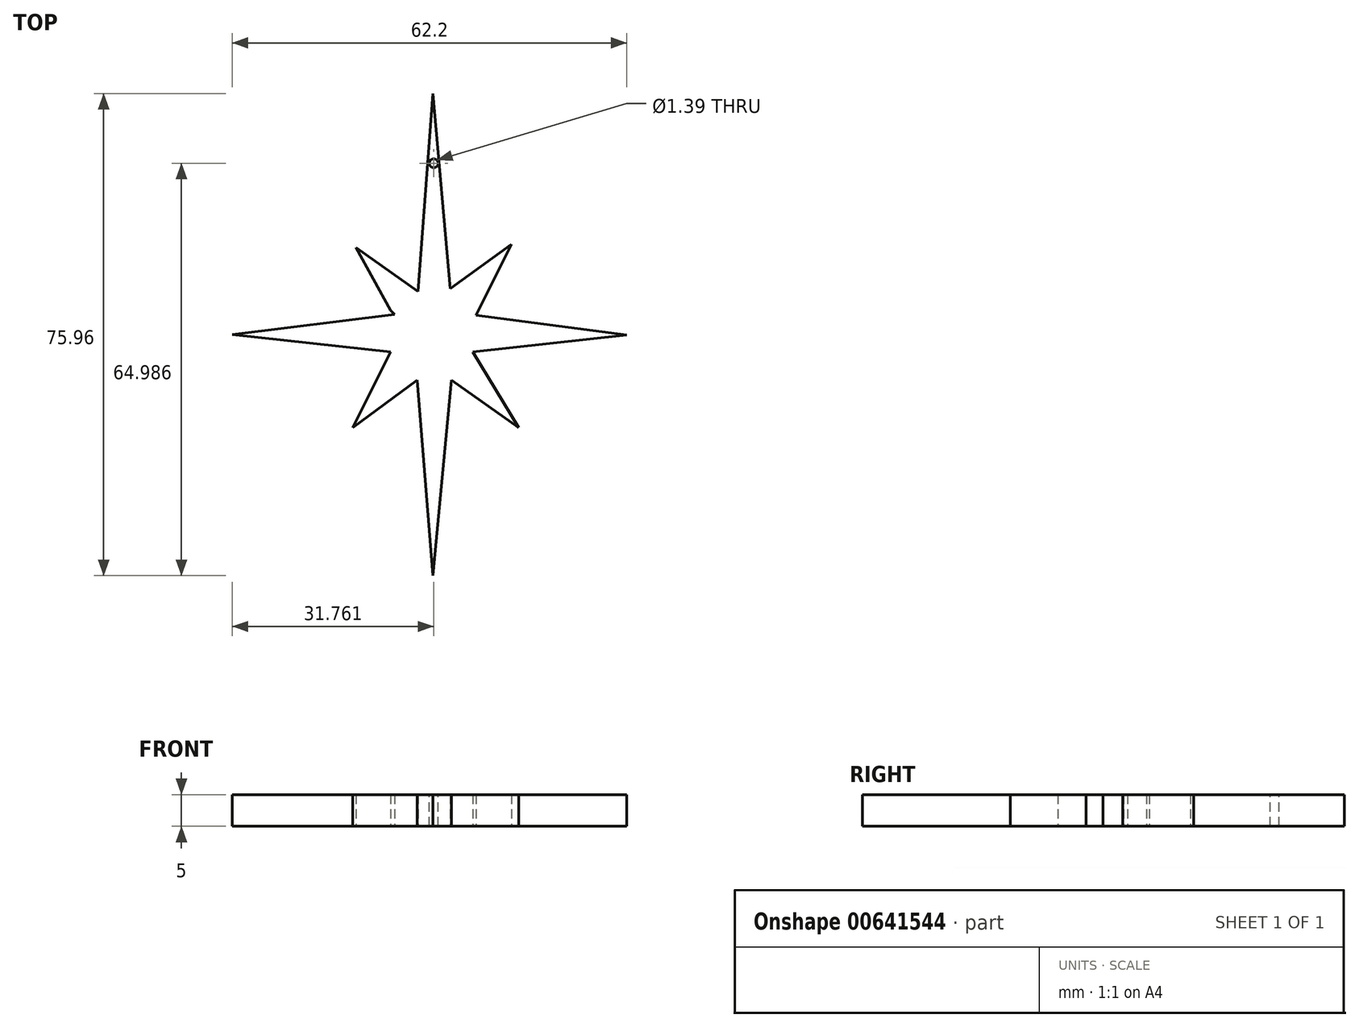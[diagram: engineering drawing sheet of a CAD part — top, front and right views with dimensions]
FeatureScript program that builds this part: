
annotation { "Feature Type Name" : "Feature", "Feature Type Description" : "" }
export const myFeature = defineFeature(function(context is Context, id is Id, definition is map)
    precondition{}
    {
        {
            var Q0;
            Q0=qCreatedBy(makeId("Top.planeOp"),FACE);
            var sketch = newSketch(context, id + "F0", { "sketchPlane" : qUnion([Q0])});
            skLineSegment(sketch, "E0", {"start": v(-31.65, 75.96) * mm, "end": v(-34, 44.76) * mm});
            skLineSegment(sketch, "E1", {"start": v(-34, 44.76) * mm, "end": v(-43.8, 51.72) * mm});
            skLineSegment(sketch, "E2", {"start": v(-43.8, 51.72) * mm, "end": v(-38.34, 41.8) * mm});
            skLineSegment(sketch, "E3", {"start": v(-38.34, 41.8) * mm, "end": v(-37.71, 41.17) * mm});
            skLineSegment(sketch, "E4", {"start": v(-37.71, 41.17) * mm, "end": v(-63.3, 37.98) * mm});
            skLineSegment(sketch, "E5", {"start": v(-63.3, 37.98) * mm, "end": v(-38.34, 35.25) * mm});
            skLineSegment(sketch, "E6", {"start": v(-38.34, 35.25) * mm, "end": v(-44.32, 23.32) * mm});
            skLineSegment(sketch, "E7", {"start": v(-44.32, 23.32) * mm, "end": v(-34.12, 30.83) * mm});
            skLineSegment(sketch, "E8", {"start": v(-34.12, 30.83) * mm, "end": v(-31.65, 0) * mm});
            skLineSegment(sketch, "E9", {"start": v(-31.65, 0) * mm, "end": v(-28.72, 30.83) * mm});
            skLineSegment(sketch, "E10", {"start": v(-28.72, 30.83) * mm, "end": v(-18.13, 23.32) * mm});
            skLineSegment(sketch, "E11", {"start": v(-18.13, 23.32) * mm, "end": v(-25.41, 35.29) * mm});
            skLineSegment(sketch, "E12", {"start": v(-25.41, 35.29) * mm, "end": v(-1.1, 37.9) * mm});
            skLineSegment(sketch, "E13", {"start": v(-1.1, 37.9) * mm, "end": v(-24.9, 41.01) * mm});
            skLineSegment(sketch, "E14", {"start": v(-24.9, 41.01) * mm, "end": v(-19.3, 52.2) * mm});
            skLineSegment(sketch, "E15", {"start": v(-19.3, 52.2) * mm, "end": v(-28.95, 45.22) * mm});
            skLineSegment(sketch, "E16", {"start": v(-28.95, 45.22) * mm, "end": v(-31.65, 75.96) * mm});
            skPoint(sketch, "E17", {"position": v(-32.9, 59.23) * mm});
            skPoint(sketch, "E18", {"position": v(-32.27, 67.76) * mm});
            skPoint(sketch, "E19", {"position": v(-39.03, 48.33) * mm});
            skPoint(sketch, "E20", {"position": v(-33.58, 50.24) * mm});
            skPoint(sketch, "E21", {"position": v(-29.3, 49.14) * mm});
            skPoint(sketch, "E22", {"position": v(-26.5, 47) * mm});
            skPoint(sketch, "E23", {"position": v(-27.45, 29.93) * mm});
            skPoint(sketch, "E24", {"position": v(-23.8, 32.64) * mm});
            skPoint(sketch, "E25", {"position": v(-38.62, 34.7) * mm});
            skPoint(sketch, "E26", {"position": v(-40.61, 35.27) * mm});
            skPoint(sketch, "E27", {"position": v(-23.1, 44.58) * mm});
            skPoint(sketch, "E28", {"position": v(-39.4, 35.37) * mm});
            skPoint(sketch, "E29", {"position": v(-43.38, 35.8) * mm});
            skPoint(sketch, "E30", {"position": v(-39.5, 32.93) * mm});
            skSolve(sketch);
        }
        {
            var Q0;
            Q0 = qSketchRegion(id + "F0", true);
            extrude(context, id + "F1", {"entities" : qUnion([Q0]), "depth" : 5 * mm, "offsetDistance" : 25 * mm});
        }
        {
            var Q0;
            Q0=makeQuery(id+"F1.opExtrude","CAP_FACE",FACE,{"disambiguationData":[OSD([sQuery(id+"F0.wireOp",EDGE,"E0"),sQuery(id+"F0.wireOp",EDGE,"E1"),sQuery(id+"F0.wireOp",EDGE,"E2"),sQuery(id+"F0.wireOp",EDGE,"E3"),sQuery(id+"F0.wireOp",EDGE,"E4"),sQuery(id+"F0.wireOp",EDGE,"E5"),sQuery(id+"F0.wireOp",EDGE,"E6"),sQuery(id+"F0.wireOp",EDGE,"E7"),sQuery(id+"F0.wireOp",EDGE,"E8"),sQuery(id+"F0.wireOp",EDGE,"E9"),sQuery(id+"F0.wireOp",EDGE,"E10"),sQuery(id+"F0.wireOp",EDGE,"E11"),sQuery(id+"F0.wireOp",EDGE,"E12"),sQuery(id+"F0.wireOp",EDGE,"E13"),sQuery(id+"F0.wireOp",EDGE,"E14"),sQuery(id+"F0.wireOp",EDGE,"E15"),sQuery(id+"F0.wireOp",EDGE,"E16")])],"isStart":false});
            var sketch = newSketch(context, id + "F2", { "sketchPlane" : qUnion([Q0])});
            skCircle(sketch, "E31", {"center": v(-31.54, 64.99) * mm, "radius": 0.7 * mm});
            skSolve(sketch);
        }
        {
            var Q0;
            Q0 = qSketchRegion(id + "F2", true);
            extrude(context, id + "F3", {"entities" : qUnion([Q0]), "operationType" : NewBodyOperationType.REMOVE, "oppositeDirection" : true, "depth" : 5 * mm, "offsetDistance" : 25 * mm});
        }
    });
